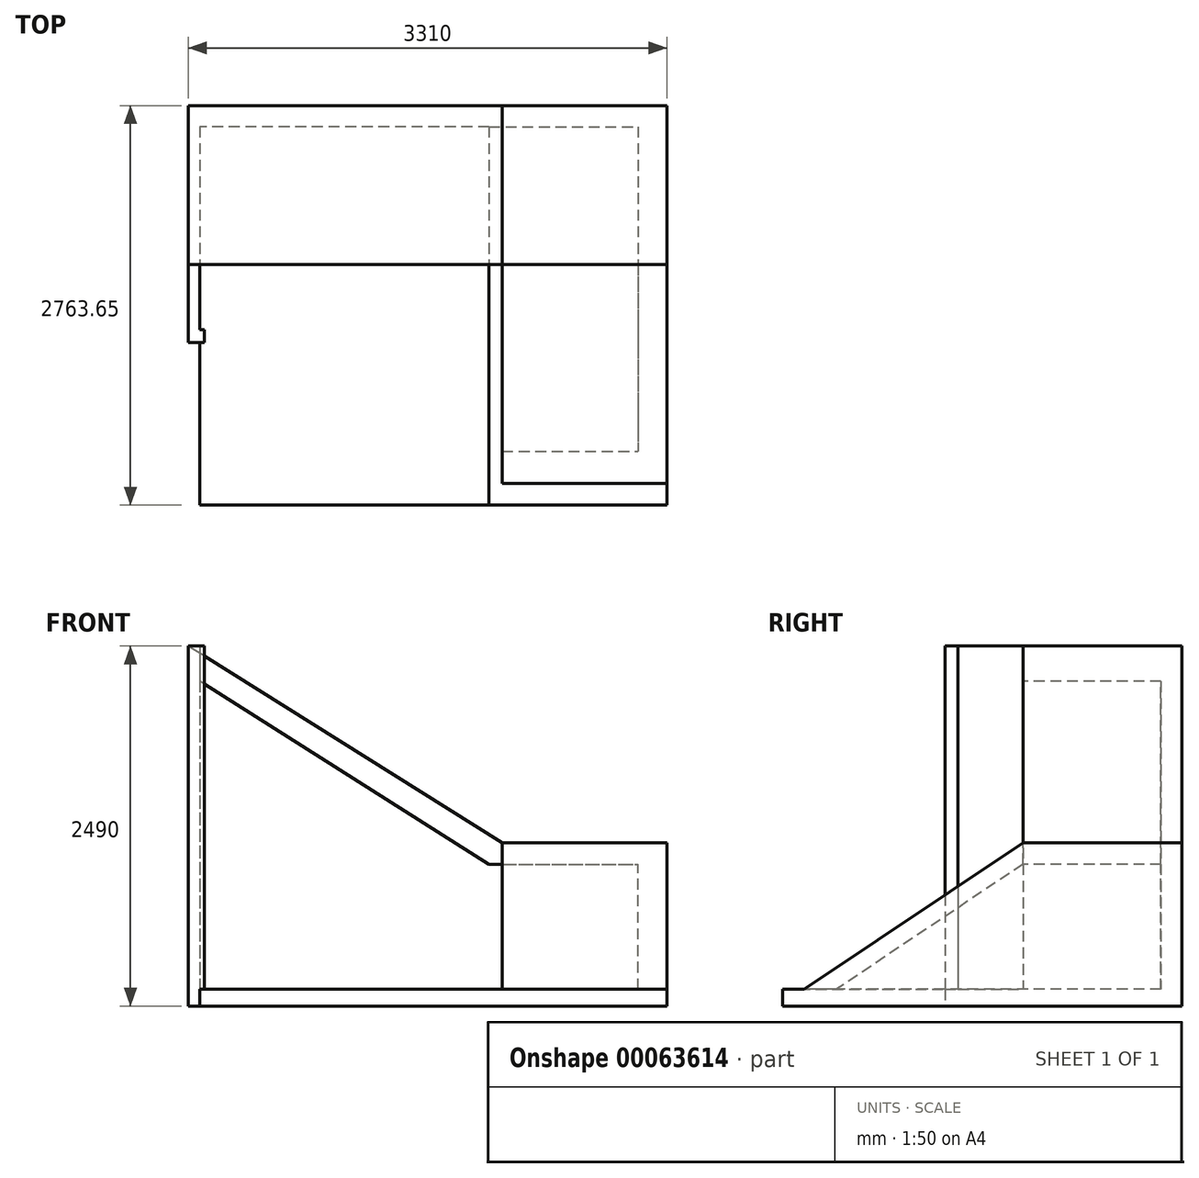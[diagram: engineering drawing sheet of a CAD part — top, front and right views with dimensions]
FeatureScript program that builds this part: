
annotation { "Feature Type Name" : "Feature", "Feature Type Description" : "" }
export const myFeature = defineFeature(function(context is Context, id is Id, definition is map)
    precondition{}
    {
        {
            var Q0;
            Q0=qCreatedBy(makeId("Front.planeOp"),FACE);
            var sketch = newSketch(context, id + "F0", { "sketchPlane" : qUnion([Q0])});
            skLineSegment(sketch, "E0", {"start": v(0, 0) * mm, "end": v(0, -2490) * mm});
            skLineSegment(sketch, "E1", {"start": v(0, -2490) * mm, "end": v(2170, -2490) * mm});
            skLineSegment(sketch, "E2", {"start": v(2170, -2490) * mm, "end": v(2170, -1360) * mm});
            skLineSegment(sketch, "E3", {"start": v(2170, -1360) * mm, "end": v(0, 0) * mm});
            skSolve(sketch);
        }
        {
            var Q0;
            Q0=makeQuery(id+"F0.imprint","IMPRINT",FACE,{"disambiguationData":[TD([[makeQuery(id+"F0.imprint","IMPRINT",EDGE,{"derivedFrom":sQuery(id+"F0.wireOp",EDGE,"E0")}),1.0]])]});
            extrude(context, id + "F1", {"entities" : qUnion([Q0]), "depth" : 1100 * mm});
        }
        {
            var Q0;
            Q0=makeQuery(id+"F1.opExtrude","CAP_FACE",FACE,{"disambiguationData":[OSD([sQuery(id+"F0.wireOp",EDGE,"E0"),sQuery(id+"F0.wireOp",EDGE,"E1"),sQuery(id+"F0.wireOp",EDGE,"E2"),sQuery(id+"F0.wireOp",EDGE,"E3")])],"isStart":false});
            var sketch = newSketch(context, id + "F2", { "sketchPlane" : qUnion([Q0])});
            skLineSegment(sketch, "E4", {"start": v(79.81, -244.3) * mm, "end": v(79.81, -2374.3) * mm});
            skLineSegment(sketch, "E5", {"start": v(79.81, -2374.3) * mm, "end": v(2079.81, -2374.3) * mm});
            skLineSegment(sketch, "E6", {"start": v(2079.81, -2374.3) * mm, "end": v(2079.81, -1509.3) * mm});
            skLineSegment(sketch, "E7", {"start": v(2079.81, -1509.3) * mm, "end": v(79.81, -244.3) * mm});
            skSolve(sketch);
        }
        {
            var Q0;
            Q0=makeQuery(id+"F2.imprint","IMPRINT",FACE,{"disambiguationData":[TD([[makeQuery(id+"F2.imprint","IMPRINT",EDGE,{"derivedFrom":sQuery(id+"F2.wireOp",EDGE,"E4")}),1.0]])]});
            extrude(context, id + "F3", {"entities" : qUnion([Q0]), "operationType" : NewBodyOperationType.REMOVE, "oppositeDirection" : true, "depth" : 955 * mm});
        }
        {
            var Q0;
            Q0=makeQuery(id+"F1.opExtrude","SWEPT_FACE",FACE,{"disambiguationData":[OSD([sQuery(id+"F0.wireOp",EDGE,"E0")])]});
            var sketch = newSketch(context, id + "F4", { "sketchPlane" : qUnion([Q0])});
            skLineSegment(sketch, "E8.bottom", {"start": v(1100, 0) * mm, "end": v(1550, 0) * mm});
            skLineSegment(sketch, "E8.top", {"start": v(1100, -2490) * mm, "end": v(1550, -2490) * mm});
            skLineSegment(sketch, "E8.left", {"start": v(1100, 0) * mm, "end": v(1100, -2490) * mm});
            skLineSegment(sketch, "E8.right", {"start": v(1550, 0) * mm, "end": v(1550, -2490) * mm});
            skSolve(sketch);
        }
        {
            var Q0;
            Q0=makeQuery(id+"F4.imprint","IMPRINT",FACE,{"disambiguationData":[TD([[makeQuery(id+"F4.imprint","IMPRINT",EDGE,{"derivedFrom":sQuery(id+"F4.wireOp",EDGE,"E8.bottom")}),-1.0]])]});
            extrude(context, id + "F5", {"entities" : qUnion([Q0]), "operationType" : NewBodyOperationType.ADD, "oppositeDirection" : true, "depth" : 80 * mm});
        }
        {
            var Q0;
            Q0=makeQuery(id+"F5.boolean.opBoolean","MERGE",FACE,{"derivedFrom":[makeQuery(id+"F1.opExtrude","SWEPT_FACE",FACE,{"disambiguationData":[OSD([sQuery(id+"F0.wireOp",EDGE,"E0")])]}),makeQuery(id+"F5.opExtrude","CAP_FACE",FACE,{"disambiguationData":[OSD([sQuery(id+"F4.wireOp",EDGE,"E8.bottom"),sQuery(id+"F4.wireOp",EDGE,"E8.top"),sQuery(id+"F4.wireOp",EDGE,"E8.left"),sQuery(id+"F4.wireOp",EDGE,"E8.right")])],"isStart":true})]});
            var sketch = newSketch(context, id + "F6", { "sketchPlane" : qUnion([Q0])});
            skLineSegment(sketch, "E9.bottom", {"start": v(1550, 0) * mm, "end": v(1640, 0) * mm});
            skLineSegment(sketch, "E9.top", {"start": v(1550, -2490) * mm, "end": v(1640, -2490) * mm});
            skLineSegment(sketch, "E9.left", {"start": v(1550, 0) * mm, "end": v(1550, -2490) * mm});
            skLineSegment(sketch, "E9.right", {"start": v(1640, 0) * mm, "end": v(1640, -2490) * mm});
            skSolve(sketch);
        }
        {
            var Q0;
            Q0=makeQuery(id+"F6.imprint","IMPRINT",FACE,{"disambiguationData":[TD([[makeQuery(id+"F6.imprint","IMPRINT",EDGE,{"derivedFrom":sQuery(id+"F6.wireOp",EDGE,"E9.bottom")}),-1.0]])]});
            extrude(context, id + "F7", {"entities" : qUnion([Q0]), "operationType" : NewBodyOperationType.ADD, "oppositeDirection" : true, "depth" : 110 * mm});
        }
        {
            var Q0;
            Q0=makeQuery(id+"F1.opExtrude","CAP_FACE",FACE,{"disambiguationData":[OSD([sQuery(id+"F0.wireOp",EDGE,"E0"),sQuery(id+"F0.wireOp",EDGE,"E1"),sQuery(id+"F0.wireOp",EDGE,"E2"),sQuery(id+"F0.wireOp",EDGE,"E3")])],"isStart":false});
            var sketch = newSketch(context, id + "F8", { "sketchPlane" : qUnion([Q0])});
            skLineSegment(sketch, "E10.bottom", {"start": v(2079.81, -1509.3) * mm, "end": v(2170, -1509.3) * mm});
            skLineSegment(sketch, "E10.top", {"start": v(2079.81, -2374.27) * mm, "end": v(2170, -2374.27) * mm});
            skLineSegment(sketch, "E10.left", {"start": v(2079.81, -1509.3) * mm, "end": v(2079.81, -2374.27) * mm});
            skLineSegment(sketch, "E10.right", {"start": v(2170, -1509.3) * mm, "end": v(2170, -2374.27) * mm});
            skSolve(sketch);
        }
        {
            var Q0;
            Q0=makeQuery(id+"F8.imprint","IMPRINT",FACE,{"disambiguationData":[TD([[makeQuery(id+"F8.imprint","IMPRINT",EDGE,{"derivedFrom":sQuery(id+"F8.wireOp",EDGE,"E10.bottom")}),-1.0]])]});
            extrude(context, id + "F9", {"entities" : qUnion([Q0]), "operationType" : NewBodyOperationType.REMOVE, "oppositeDirection" : true, "depth" : 955 * mm});
        }
        {
            var Q0;
            Q0=makeQuery(id+"F1.opExtrude","SWEPT_FACE",FACE,{"disambiguationData":[OSD([sQuery(id+"F0.wireOp",EDGE,"E2")])]});
            extrude(context, id + "F10", {"entities" : qUnion([Q0]), "operationType" : NewBodyOperationType.ADD, "depth" : 940 * mm});
        }
        {
            var Q0;
            {var subQ0=sQuery(id+"F0.wireOp",EDGE,"E2");var subQ4=sQuery(id+"F0.wireOp",EDGE,"E1");var subQ5=makeQuery(id+"F1.opExtrude","SWEPT_FACE",FACE,{"disambiguationData":[OSD([subQ4])]});var subQ7=makeQuery(id+"F1.opExtrude","CAP_FACE",FACE,{"disambiguationData":[OSD([sQuery(id+"F0.wireOp",EDGE,"E0"),subQ4,subQ0,sQuery(id+"F0.wireOp",EDGE,"E3")])],"isStart":false});Q0=makeQuery(id+"F10.boolean.opBoolean","MERGE",FACE,{"derivedFrom":[makeQuery(id+"F9.boolean.opBoolean","SPLIT",FACE,{"disambiguationData":[TD([subQ5])],"derivedFrom":subQ7}),makeQuery(id+"F10.opExtrude","SWEPT_FACE",FACE,{"disambiguationData":[OSD([subQ0]),TDD([makeQuery(id+"F9.boolean.opBoolean","SPLIT",EDGE,{"disambiguationData":[TD([subQ5])],"derivedFrom":makeQuery(id+"F1.opExtrude","CAP_EDGE",EDGE,{"disambiguationData":[OSD([subQ0])],"isStart":false})})])]})]});}
            extrude(context, id + "F11", {"entities" : qUnion([Q0]), "operationType" : NewBodyOperationType.ADD, "depth" : 1290 * mm});
        }
        {
            var Q0;
            {var subQ0=sQuery(id+"F0.wireOp",EDGE,"E2");Q0=makeQuery(id+"F11.boolean.opBoolean","MERGE",FACE,{"derivedFrom":[makeQuery(id+"F10.opExtrude","CAP_FACE",FACE,{"disambiguationData":[OSD([subQ0])],"isStart":false}),makeQuery(id+"F11.opExtrude","SWEPT_FACE",FACE,{"disambiguationData":[OSD([subQ0])]})]});}
            var sketch = newSketch(context, id + "F12", { "sketchPlane" : qUnion([Q0])});
            skLineSegment(sketch, "E11", {"start": v(-1100, -1509.3) * mm, "end": v(-2390, -2374.27) * mm});
            skLineSegment(sketch, "E12", {"start": v(-1100, -1360) * mm, "end": v(-2619.97, -2379.18) * mm});
            skLineSegment(sketch, "E13", {"start": v(-2390, -2374.27) * mm, "end": v(-2619.97, -2379.18) * mm});
            skSolve(sketch);
        }
        {
            var Q0;
            Q0=makeQuery(id+"F12.imprint","IMPRINT",FACE,{"disambiguationData":[TD([[makeQuery(id+"F12.imprint","IMPRINT",EDGE,{"derivedFrom":sQuery(id+"F12.wireOp",EDGE,"E11")}),-1.0]])]});
            extrude(context, id + "F13", {"entities" : qUnion([Q0]), "oppositeDirection" : true, "depth" : 940 * mm});
        }
        {
            var Q0;
            Q0=makeQuery(id+"F11.opExtrude","CAP_FACE",FACE,{"disambiguationData":[OSD([sQuery(id+"F0.wireOp",EDGE,"E0"),sQuery(id+"F0.wireOp",EDGE,"E1"),sQuery(id+"F0.wireOp",EDGE,"E2"),sQuery(id+"F0.wireOp",EDGE,"E3")])],"isStart":false});
            extrude(context, id + "F14", {"entities" : qUnion([Q0]), "operationType" : NewBodyOperationType.ADD, "depth" : 373.65 * mm});
        }
        {
            var Q0;
            {var subQ0=sQuery(id+"F0.wireOp",EDGE,"E2");Q0=makeQuery(id+"F14.boolean.opBoolean","MERGE",FACE,{"derivedFrom":[makeQuery(id+"F11.boolean.opBoolean","MERGE",FACE,{"derivedFrom":[makeQuery(id+"F10.opExtrude","CAP_FACE",FACE,{"disambiguationData":[OSD([subQ0])],"isStart":false}),makeQuery(id+"F11.opExtrude","SWEPT_FACE",FACE,{"disambiguationData":[OSD([subQ0])]})]}),makeQuery(id+"F13.opExtrude","CAP_FACE",FACE,{"disambiguationData":[OSD([subQ0,sQuery(id+"F12.wireOp",EDGE,"E11"),sQuery(id+"F12.wireOp",EDGE,"E12"),sQuery(id+"F12.wireOp",EDGE,"E13")])],"isStart":true}),makeQuery(id+"F14.opExtrude","SWEPT_FACE",FACE,{"disambiguationData":[OSD([subQ0])]})]});}
            var sketch = newSketch(context, id + "F15", { "sketchPlane" : qUnion([Q0])});
            skLineSegment(sketch, "E14", {"start": v(0, -1360) * mm, "end": v(0, -2490) * mm});
            skLineSegment(sketch, "E15", {"start": v(0, -2490) * mm, "end": v(-2763.65, -2490) * mm});
            skLineSegment(sketch, "E16", {"start": v(-2763.65, -2490) * mm, "end": v(-2763.65, -2374.27) * mm});
            skLineSegment(sketch, "E17", {"start": v(-2763.65, -2374.27) * mm, "end": v(-2612.65, -2374.27) * mm});
            skLineSegment(sketch, "E18", {"start": v(-2612.65, -2374.27) * mm, "end": v(-1100, -1360) * mm});
            skLineSegment(sketch, "E19", {"start": v(-1100, -1360) * mm, "end": v(0, -1360) * mm});
            skSolve(sketch);
        }
        {
            var Q0;
            Q0 = qSketchRegion(id + "F15", true);
            extrude(context, id + "F16", {"entities" : qUnion([Q0]), "operationType" : NewBodyOperationType.ADD, "depth" : 200 * mm});
        }
    });
